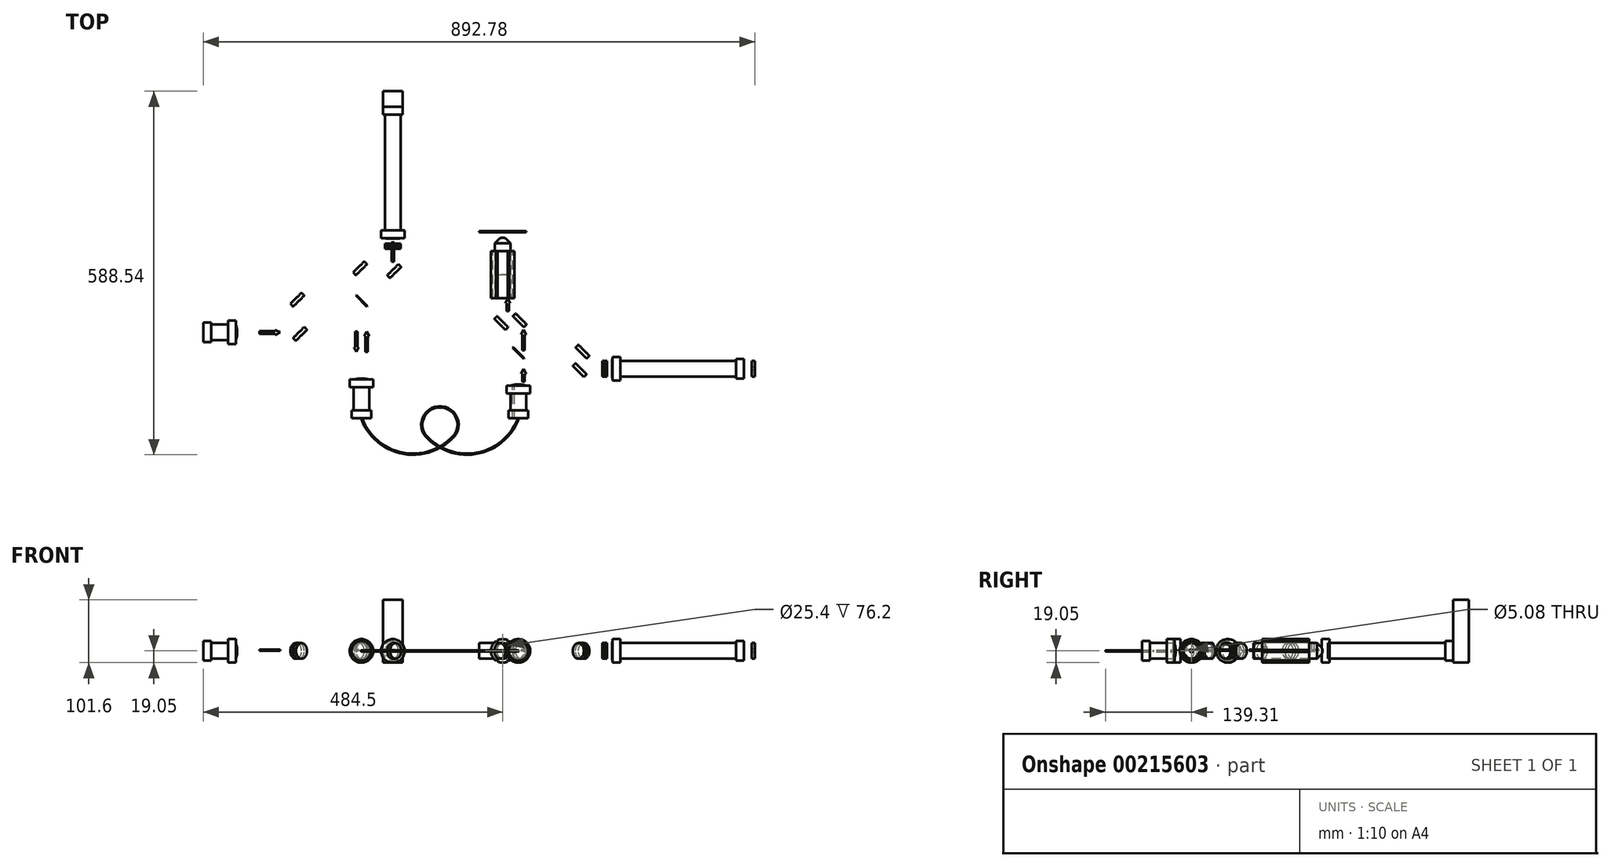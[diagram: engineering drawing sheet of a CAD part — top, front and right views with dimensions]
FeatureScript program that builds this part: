
annotation { "Feature Type Name" : "Feature", "Feature Type Description" : "" }
export const myFeature = defineFeature(function(context is Context, id is Id, definition is map)
    precondition{}
    {
        {
            var Q0;
            Q0=qCreatedBy(makeId("Top.planeOp"),FACE);
            var sketch = newSketch(context, id + "F0", { "sketchPlane" : qUnion([Q0])});
            skLineSegment(sketch, "E0", {"start": v(-101.6, 0) * mm, "end": v(0, 0) * mm, "construction": true});
            skLineSegment(sketch, "E1", {"start": v(0, 0) * mm, "end": v(0, 50.8) * mm});
            skLineSegment(sketch, "E2", {"start": v(0, 50.8) * mm, "end": v(101.6, 50.8) * mm});
            skLineSegment(sketch, "E3", {"start": v(101.6, 50.8) * mm, "end": v(101.6, -76.2) * mm, "construction": true});
            skLineSegment(sketch, "E4", {"start": v(101.6, 50.8) * mm, "end": v(101.6, 101.6) * mm, "construction": true});
            skLineSegment(sketch, "E5", {"start": v(101.6, 101.6) * mm, "end": v(152.4, 101.6) * mm, "construction": true});
            skLineSegment(sketch, "E6", {"start": v(152.4, 101.6) * mm, "end": v(152.4, 152.4) * mm, "construction": true});
            skLineSegment(sketch, "E7.bottom", {"start": v(-114.3, 19.05) * mm, "end": v(-101.6, 19.05) * mm});
            skLineSegment(sketch, "E7.top", {"start": v(-114.3, -19.05) * mm, "end": v(-101.6, -19.05) * mm, "construction": true});
            skLineSegment(sketch, "E7.left", {"start": v(-114.3, 19.05) * mm, "end": v(-114.3, -19.05) * mm, "construction": true});
            skLineSegment(sketch, "E7.right", {"start": v(-101.6, 19.05) * mm, "end": v(-101.6, -19.05) * mm, "construction": true});
            skLineSegment(sketch, "E8.bottom", {"start": v(-114.3, 12.7) * mm, "end": v(-141.6, 12.7) * mm});
            skLineSegment(sketch, "E8.top", {"start": v(-114.3, -12.7) * mm, "end": v(-141.6, -12.7) * mm, "construction": true});
            skLineSegment(sketch, "E8.left", {"start": v(-114.3, 12.7) * mm, "end": v(-114.3, -12.7) * mm});
            skLineSegment(sketch, "E8.right", {"start": v(-141.6, 12.7) * mm, "end": v(-141.6, -12.7) * mm});
            skLineSegment(sketch, "E9.bottom", {"start": v(-154.3, 15.88) * mm, "end": v(-141.6, 15.88) * mm});
            skLineSegment(sketch, "E9.top", {"start": v(-154.3, -15.87) * mm, "end": v(-141.6, -15.87) * mm, "construction": true});
            skLineSegment(sketch, "E9.left", {"start": v(-154.3, 15.88) * mm, "end": v(-154.3, -15.87) * mm, "construction": true});
            skLineSegment(sketch, "E9.right", {"start": v(-141.6, 15.88) * mm, "end": v(-141.6, -15.87) * mm, "construction": true});
            skLineSegment(sketch, "E10.bottom", {"start": v(82.55, -88.9) * mm, "end": v(82.55, -76.2) * mm, "construction": true});
            skLineSegment(sketch, "E10.top", {"start": v(120.65, -88.9) * mm, "end": v(120.65, -76.2) * mm, "construction": true});
            skLineSegment(sketch, "E10.left", {"start": v(82.55, -88.9) * mm, "end": v(120.65, -88.9) * mm, "construction": true});
            skLineSegment(sketch, "E10.right", {"start": v(82.55, -76.2) * mm, "end": v(120.65, -76.2) * mm, "construction": true});
            skLineSegment(sketch, "E11.bottom", {"start": v(88.9, -88.9) * mm, "end": v(88.9, -126.2) * mm, "construction": true});
            skLineSegment(sketch, "E11.top", {"start": v(114.3, -88.9) * mm, "end": v(114.3, -126.2) * mm, "construction": true});
            skLineSegment(sketch, "E11.left", {"start": v(88.9, -88.9) * mm, "end": v(114.3, -88.9) * mm, "construction": true});
            skLineSegment(sketch, "E11.right", {"start": v(88.9, -126.2) * mm, "end": v(114.3, -126.2) * mm, "construction": true});
            skLineSegment(sketch, "E12.bottom", {"start": v(85.73, -138.9) * mm, "end": v(85.73, -126.2) * mm, "construction": true});
            skLineSegment(sketch, "E12.top", {"start": v(117.48, -138.9) * mm, "end": v(117.48, -126.2) * mm, "construction": true});
            skLineSegment(sketch, "E12.left", {"start": v(85.73, -138.9) * mm, "end": v(117.48, -138.9) * mm, "construction": true});
            skLineSegment(sketch, "E12.right", {"start": v(85.73, -126.2) * mm, "end": v(117.48, -126.2) * mm, "construction": true});
            skLineSegment(sketch, "E13.bottom", {"start": v(-8.98, -8.98) * mm, "end": v(8.98, 8.98) * mm});
            skLineSegment(sketch, "E13.top", {"start": v(-6.74, -11.23) * mm, "end": v(11.23, 6.74) * mm});
            skLineSegment(sketch, "E13.left", {"start": v(-8.98, -8.98) * mm, "end": v(-6.74, -11.23) * mm});
            skLineSegment(sketch, "E13.right", {"start": v(8.98, 8.98) * mm, "end": v(11.23, 6.74) * mm});
            skLineSegment(sketch, "E14.bottom", {"start": v(-11.23, 44.06) * mm, "end": v(6.74, 62.03) * mm});
            skLineSegment(sketch, "E14.top", {"start": v(-8.98, 41.82) * mm, "end": v(8.98, 59.78) * mm});
            skLineSegment(sketch, "E14.left", {"start": v(-11.23, 44.06) * mm, "end": v(-8.98, 41.82) * mm});
            skLineSegment(sketch, "E14.right", {"start": v(6.74, 62.03) * mm, "end": v(8.98, 59.78) * mm});
            skLineSegment(sketch, "E15.bottom", {"start": v(93.33, 60.49) * mm, "end": v(111.29, 42.53) * mm});
            skLineSegment(sketch, "E15.top", {"start": v(92.62, 59.78) * mm, "end": v(110.58, 41.82) * mm});
            skLineSegment(sketch, "E15.left", {"start": v(93.33, 60.49) * mm, "end": v(92.62, 59.78) * mm});
            skLineSegment(sketch, "E15.right", {"start": v(111.29, 42.53) * mm, "end": v(110.58, 41.82) * mm});
            skLineSegment(sketch, "E16.bottom", {"start": v(90.37, 94.86) * mm, "end": v(108.34, 112.83) * mm});
            skLineSegment(sketch, "E16.top", {"start": v(92.62, 92.62) * mm, "end": v(110.58, 110.58) * mm});
            skLineSegment(sketch, "E16.left", {"start": v(90.37, 94.86) * mm, "end": v(92.62, 92.62) * mm});
            skLineSegment(sketch, "E16.right", {"start": v(108.34, 112.83) * mm, "end": v(110.58, 110.58) * mm});
            skLineSegment(sketch, "E17.bottom", {"start": v(143.42, 92.62) * mm, "end": v(161.38, 110.58) * mm});
            skLineSegment(sketch, "E17.top", {"start": v(145.66, 90.37) * mm, "end": v(163.63, 108.34) * mm});
            skLineSegment(sketch, "E17.left", {"start": v(143.42, 92.62) * mm, "end": v(145.66, 90.37) * mm});
            skLineSegment(sketch, "E17.right", {"start": v(161.38, 110.58) * mm, "end": v(163.63, 108.34) * mm});
            skLineSegment(sketch, "E18.bottom", {"start": v(171.45, 165.1) * mm, "end": v(171.45, 152.4) * mm, "construction": true});
            skLineSegment(sketch, "E18.top", {"start": v(133.35, 165.1) * mm, "end": v(133.35, 152.4) * mm});
            skLineSegment(sketch, "E18.left", {"start": v(171.45, 165.1) * mm, "end": v(133.35, 165.1) * mm, "construction": true});
            skLineSegment(sketch, "E18.right", {"start": v(171.45, 152.4) * mm, "end": v(133.35, 152.4) * mm, "construction": true});
            skLineSegment(sketch, "E19.bottom", {"start": v(165.1, 165.1) * mm, "end": v(165.1, 352.4) * mm, "construction": true});
            skLineSegment(sketch, "E19.top", {"start": v(139.7, 165.1) * mm, "end": v(139.7, 352.4) * mm, "construction": true});
            skLineSegment(sketch, "E19.left", {"start": v(165.1, 165.1) * mm, "end": v(139.7, 165.1) * mm, "construction": true});
            skLineSegment(sketch, "E19.right", {"start": v(165.1, 352.4) * mm, "end": v(139.7, 352.4) * mm, "construction": true});
            skLineSegment(sketch, "E20.bottom", {"start": v(168.28, 365.1) * mm, "end": v(168.28, 352.4) * mm, "construction": true});
            skLineSegment(sketch, "E20.top", {"start": v(136.53, 365.1) * mm, "end": v(136.53, 352.4) * mm, "construction": true});
            skLineSegment(sketch, "E20.left", {"start": v(168.28, 365.1) * mm, "end": v(136.53, 365.1) * mm, "construction": true});
            skLineSegment(sketch, "E20.right", {"start": v(168.28, 352.4) * mm, "end": v(136.53, 352.4) * mm, "construction": true});
            skLineSegment(sketch, "E21", {"start": v(-101.6, 0) * mm, "end": v(-101.6, 19.05) * mm, "construction": true});
            skLineSegment(sketch, "E22", {"start": v(-101.6, 0) * mm, "end": v(-101.6, 19.05) * mm});
            skLineSegment(sketch, "E23", {"start": v(-114.3, 12.7) * mm, "end": v(-114.3, 19.05) * mm});
            skLineSegment(sketch, "E24", {"start": v(-154.3, 15.88) * mm, "end": v(-154.3, 0) * mm});
            skLineSegment(sketch, "E25", {"start": v(-154.3, 0) * mm, "end": v(-101.6, 0) * mm});
            skLineSegment(sketch, "E26", {"start": v(-141.6, 15.88) * mm, "end": v(-141.6, 12.7) * mm});
            skArc(sketch, "E27", {"start": v(-101.6, -12.7) * mm, "mid": v(-99.53, 0) * mm, "end": v(-101.6, 12.7) * mm, "construction": true});
            skArc(sketch, "E28", {"start": v(-99.53, 0) * mm, "mid": v(-100.05, 6.43) * mm, "end": v(-101.6, 12.7) * mm});
            skLineSegment(sketch, "E29", {"start": v(-99.53, 0) * mm, "end": v(-101.6, 0) * mm});
            skLineSegment(sketch, "E30", {"start": v(101.6, -76.2) * mm, "end": v(120.65, -76.2) * mm, "construction": true});
            skLineSegment(sketch, "E31", {"start": v(120.65, -88.9) * mm, "end": v(114.3, -88.9) * mm, "construction": true});
            skLineSegment(sketch, "E32", {"start": v(101.6, -76.2) * mm, "end": v(120.65, -76.2) * mm});
            skLineSegment(sketch, "E33", {"start": v(120.65, -88.9) * mm, "end": v(114.3, -88.9) * mm});
            skLineSegment(sketch, "E34", {"start": v(114.3, -126.2) * mm, "end": v(114.3, -88.9) * mm});
            skLineSegment(sketch, "E35", {"start": v(114.3, -88.9) * mm, "end": v(120.65, -88.9) * mm});
            skLineSegment(sketch, "E36", {"start": v(120.65, -88.9) * mm, "end": v(120.65, -76.2) * mm});
            skLineSegment(sketch, "E37", {"start": v(114.3, -126.2) * mm, "end": v(117.48, -126.2) * mm});
            skLineSegment(sketch, "E38", {"start": v(117.48, -126.2) * mm, "end": v(117.48, -138.9) * mm});
            skLineSegment(sketch, "E39", {"start": v(117.48, -138.9) * mm, "end": v(101.6, -138.9) * mm});
            skLineSegment(sketch, "E40", {"start": v(101.6, -76.2) * mm, "end": v(101.6, -138.9) * mm});
            skArc(sketch, "E41", {"start": v(114.3, -76.2) * mm, "mid": v(101.6, -74.56) * mm, "end": v(88.9, -76.2) * mm, "construction": true});
            skArc(sketch, "E42", {"start": v(114.3, -76.2) * mm, "mid": v(108, -74.97) * mm, "end": v(101.6, -74.56) * mm});
            skLineSegment(sketch, "E43", {"start": v(101.6, -74.56) * mm, "end": v(101.6, -76.2) * mm});
            skArc(sketch, "E44", {"start": v(152.4, 152) * mm, "mid": v(158.75, 152.1) * mm, "end": v(165.1, 152.4) * mm});
            skLineSegment(sketch, "E45", {"start": v(152.4, 152.4) * mm, "end": v(152.4, 156.02) * mm, "construction": true});
            skLineSegment(sketch, "E46", {"start": v(152.4, 487.9) * mm, "end": v(152.4, 156.02) * mm, "construction": true});
            skLineSegment(sketch, "E47", {"start": v(152.4, 152) * mm, "end": v(152.4, 365.1) * mm});
            skLineSegment(sketch, "E48", {"start": v(152.4, 365.1) * mm, "end": v(168.28, 365.1) * mm});
            skLineSegment(sketch, "E49", {"start": v(168.28, 365.1) * mm, "end": v(168.28, 352.4) * mm});
            skLineSegment(sketch, "E50", {"start": v(168.28, 352.4) * mm, "end": v(165.1, 352.4) * mm});
            skLineSegment(sketch, "E51", {"start": v(165.1, 352.4) * mm, "end": v(165.1, 165.1) * mm});
            skLineSegment(sketch, "E52", {"start": v(165.1, 165.1) * mm, "end": v(171.45, 165.1) * mm});
            skLineSegment(sketch, "E53", {"start": v(171.45, 165.1) * mm, "end": v(171.45, 152.4) * mm});
            skLineSegment(sketch, "E54", {"start": v(171.45, 152.4) * mm, "end": v(165.1, 152.4) * mm});
            skLineSegment(sketch, "E55", {"start": v(101.6, -138.9) * mm, "end": v(101.6, -164.3) * mm, "construction": true});
            skLineSegment(sketch, "E56", {"start": v(101.6, -164.3) * mm, "end": v(355.6, -164.3) * mm, "construction": true});
            skLineSegment(sketch, "E57", {"start": v(355.6, -164.3) * mm, "end": v(355.6, -138.9) * mm, "construction": true});
            skLineSegment(sketch, "E58.bottom", {"start": v(336.55, -98.9) * mm, "end": v(336.55, -86.2) * mm, "construction": true});
            skLineSegment(sketch, "E58.top", {"start": v(374.65, -98.9) * mm, "end": v(374.65, -86.2) * mm, "construction": true});
            skLineSegment(sketch, "E58.left", {"start": v(336.55, -98.9) * mm, "end": v(374.65, -98.9) * mm, "construction": true});
            skLineSegment(sketch, "E58.right", {"start": v(336.55, -86.2) * mm, "end": v(374.65, -86.2) * mm, "construction": true});
            skLineSegment(sketch, "E59.bottom", {"start": v(342.9, -98.9) * mm, "end": v(342.9, -126.2) * mm, "construction": true});
            skLineSegment(sketch, "E59.top", {"start": v(368.3, -98.9) * mm, "end": v(368.3, -126.2) * mm, "construction": true});
            skLineSegment(sketch, "E59.left", {"start": v(342.9, -98.9) * mm, "end": v(368.3, -98.9) * mm, "construction": true});
            skLineSegment(sketch, "E59.right", {"start": v(342.9, -126.2) * mm, "end": v(368.3, -126.2) * mm, "construction": true});
            skLineSegment(sketch, "E60.bottom", {"start": v(339.73, -138.9) * mm, "end": v(339.73, -126.2) * mm, "construction": true});
            skLineSegment(sketch, "E60.top", {"start": v(371.48, -138.9) * mm, "end": v(371.48, -126.2) * mm, "construction": true});
            skLineSegment(sketch, "E60.left", {"start": v(339.73, -138.9) * mm, "end": v(371.48, -138.9) * mm, "construction": true});
            skLineSegment(sketch, "E60.right", {"start": v(339.73, -126.2) * mm, "end": v(371.48, -126.2) * mm, "construction": true});
            skLineSegment(sketch, "E61", {"start": v(355.6, -86.2) * mm, "end": v(374.65, -86.2) * mm, "construction": true});
            skLineSegment(sketch, "E62", {"start": v(374.65, -98.9) * mm, "end": v(368.3, -98.9) * mm, "construction": true});
            skLineSegment(sketch, "E63", {"start": v(355.6, -86.2) * mm, "end": v(374.65, -86.2) * mm});
            skLineSegment(sketch, "E64", {"start": v(374.65, -98.9) * mm, "end": v(368.3, -98.9) * mm});
            skLineSegment(sketch, "E65", {"start": v(368.3, -126.2) * mm, "end": v(368.3, -98.9) * mm});
            skLineSegment(sketch, "E66", {"start": v(368.3, -98.9) * mm, "end": v(374.65, -98.9) * mm});
            skLineSegment(sketch, "E67", {"start": v(374.65, -98.9) * mm, "end": v(374.65, -86.2) * mm});
            skLineSegment(sketch, "E68", {"start": v(368.3, -126.2) * mm, "end": v(371.48, -126.2) * mm});
            skLineSegment(sketch, "E69", {"start": v(371.48, -126.2) * mm, "end": v(371.48, -138.9) * mm});
            skLineSegment(sketch, "E70", {"start": v(371.48, -138.9) * mm, "end": v(355.6, -138.9) * mm});
            skLineSegment(sketch, "E71", {"start": v(355.6, -86.2) * mm, "end": v(355.6, -138.9) * mm});
            skArc(sketch, "E72", {"start": v(368.3, -86.2) * mm, "mid": v(355.6, -84.13) * mm, "end": v(342.9, -86.2) * mm, "construction": true});
            skArc(sketch, "E73", {"start": v(368.3, -86.2) * mm, "mid": v(362.03, -84.65) * mm, "end": v(355.6, -84.13) * mm});
            skLineSegment(sketch, "E74", {"start": v(355.6, -84.13) * mm, "end": v(355.6, -86.2) * mm});
            skLineSegment(sketch, "E75", {"start": v(355.6, -84.13) * mm, "end": v(355.6, -33.33) * mm, "construction": true});
            skLineSegment(sketch, "E76", {"start": v(355.6, -33.33) * mm, "end": v(457.2, -33.33) * mm, "construction": true});
            skLineSegment(sketch, "E77", {"start": v(457.2, -33.33) * mm, "end": v(457.2, -58.73) * mm, "construction": true});
            skLineSegment(sketch, "E78", {"start": v(457.2, -58.73) * mm, "end": v(508, -58.73) * mm, "construction": true});
            skLineSegment(sketch, "E79", {"start": v(355.6, -33.33) * mm, "end": v(355.6, 17.47) * mm, "construction": true});
            skLineSegment(sketch, "E80", {"start": v(355.6, 17.47) * mm, "end": v(330.2, 17.47) * mm, "construction": true});
            skLineSegment(sketch, "E81", {"start": v(330.2, 17.47) * mm, "end": v(330.2, 220.67) * mm, "construction": true});
            skLineSegment(sketch, "E82.bottom", {"start": v(520.7, -77.78) * mm, "end": v(508, -77.78) * mm, "construction": true});
            skLineSegment(sketch, "E82.top", {"start": v(520.7, -39.68) * mm, "end": v(508, -39.68) * mm});
            skLineSegment(sketch, "E82.left", {"start": v(520.7, -77.78) * mm, "end": v(520.7, -39.68) * mm, "construction": true});
            skLineSegment(sketch, "E82.right", {"start": v(508, -77.78) * mm, "end": v(508, -39.68) * mm, "construction": true});
            skLineSegment(sketch, "E83.bottom", {"start": v(520.7, -71.43) * mm, "end": v(708, -71.43) * mm, "construction": true});
            skLineSegment(sketch, "E83.top", {"start": v(520.7, -46.03) * mm, "end": v(708, -46.03) * mm, "construction": true});
            skLineSegment(sketch, "E83.left", {"start": v(520.7, -71.43) * mm, "end": v(520.7, -46.03) * mm, "construction": true});
            skLineSegment(sketch, "E83.right", {"start": v(708, -71.43) * mm, "end": v(708, -46.03) * mm, "construction": true});
            skLineSegment(sketch, "E84.bottom", {"start": v(720.7, -74.6) * mm, "end": v(708, -74.6) * mm, "construction": true});
            skLineSegment(sketch, "E84.top", {"start": v(720.7, -42.86) * mm, "end": v(708, -42.86) * mm, "construction": true});
            skLineSegment(sketch, "E84.left", {"start": v(720.7, -74.6) * mm, "end": v(720.7, -42.86) * mm, "construction": true});
            skLineSegment(sketch, "E84.right", {"start": v(708, -74.6) * mm, "end": v(708, -42.86) * mm, "construction": true});
            skLineSegment(sketch, "E85", {"start": v(720.7, -58.73) * mm, "end": v(720.7, -74.6) * mm});
            skLineSegment(sketch, "E86", {"start": v(720.7, -74.6) * mm, "end": v(708, -74.6) * mm});
            skLineSegment(sketch, "E87", {"start": v(708, -74.6) * mm, "end": v(708, -71.43) * mm});
            skLineSegment(sketch, "E88", {"start": v(708, -71.43) * mm, "end": v(520.7, -71.43) * mm});
            skLineSegment(sketch, "E89", {"start": v(520.7, -71.43) * mm, "end": v(520.7, -77.78) * mm});
            skLineSegment(sketch, "E90", {"start": v(520.7, -77.78) * mm, "end": v(508, -77.78) * mm});
            skArc(sketch, "E91", {"start": v(507.1, -58.73) * mm, "mid": v(507.32, -68.27) * mm, "end": v(508, -77.78) * mm});
            skLineSegment(sketch, "E92", {"start": v(508, -58.73) * mm, "end": v(765.02, -58.73) * mm, "construction": true});
            skLineSegment(sketch, "E93", {"start": v(508, -58.73) * mm, "end": v(507.1, -58.73) * mm});
            skLineSegment(sketch, "E94", {"start": v(720.7, -58.73) * mm, "end": v(507.1, -58.73) * mm});
            skLineSegment(sketch, "E95", {"start": v(448.22, -24.35) * mm, "end": v(466.18, -42.31) * mm});
            skLineSegment(sketch, "E96", {"start": v(448.22, -49.75) * mm, "end": v(466.18, -67.71) * mm});
            skLineSegment(sketch, "E97", {"start": v(364.58, -42.31) * mm, "end": v(346.62, -24.35) * mm});
            skLineSegment(sketch, "E98", {"start": v(346.62, 26.45) * mm, "end": v(364.58, 8.49) * mm});
            skLineSegment(sketch, "E99", {"start": v(321.22, 26.45) * mm, "end": v(339.18, 8.49) * mm});
            skLineSegment(sketch, "E100.bottom", {"start": v(342.9, 131.77) * mm, "end": v(317.5, 131.77) * mm});
            skLineSegment(sketch, "E100.top", {"start": v(342.9, 55.57) * mm, "end": v(317.5, 55.57) * mm});
            skLineSegment(sketch, "E100.left", {"start": v(342.9, 131.77) * mm, "end": v(342.9, 55.57) * mm});
            skLineSegment(sketch, "E100.right", {"start": v(317.5, 131.77) * mm, "end": v(317.5, 55.57) * mm});
            skPoint(sketch, "E100.middle", {"position": v(330.2, 93.67) * mm});
            skLineSegment(sketch, "E101.bottom", {"start": v(349.25, 131.77) * mm, "end": v(311.15, 131.77) * mm});
            skLineSegment(sketch, "E101.top", {"start": v(349.25, 55.57) * mm, "end": v(311.15, 55.57) * mm});
            skLineSegment(sketch, "E101.left", {"start": v(349.25, 131.77) * mm, "end": v(349.25, 55.57) * mm});
            skLineSegment(sketch, "E101.right", {"start": v(311.15, 131.77) * mm, "end": v(311.15, 55.57) * mm});
            skLineSegment(sketch, "E102.bottom", {"start": v(342.9, 93.67) * mm, "end": v(317.5, 93.67) * mm, "construction": true});
            skLineSegment(sketch, "E102.top", {"start": v(342.9, 144.47) * mm, "end": v(317.5, 144.47) * mm, "construction": true});
            skLineSegment(sketch, "E102.left", {"start": v(342.9, 93.67) * mm, "end": v(342.9, 144.47) * mm, "construction": true});
            skLineSegment(sketch, "E102.right", {"start": v(317.5, 93.67) * mm, "end": v(317.5, 144.47) * mm, "construction": true});
            skPoint(sketch, "E102.middle", {"position": v(330.2, 119.07) * mm});
            skLineSegment(sketch, "E103", {"start": v(317.5, 144.47) * mm, "end": v(323.91, 150.88) * mm, "construction": true});
            skLineSegment(sketch, "E104", {"start": v(336.49, 150.88) * mm, "end": v(342.9, 144.47) * mm, "construction": true});
            skPoint(sketch, "E105.visualSharp", {"position": v(330.2, 157.17) * mm});
            skArc(sketch, "E105.filletArc", {"start": v(336.49, 150.88) * mm, "mid": v(330.2, 153.49) * mm, "end": v(323.91, 150.88) * mm, "construction": true});
            skLineSegment(sketch, "E106", {"start": v(330.2, 93.67) * mm, "end": v(317.5, 93.67) * mm});
            skLineSegment(sketch, "E107", {"start": v(317.5, 93.67) * mm, "end": v(317.5, 144.47) * mm});
            skLineSegment(sketch, "E108", {"start": v(317.5, 144.47) * mm, "end": v(323.91, 150.88) * mm});
            skArc(sketch, "E109", {"start": v(330.2, 153.49) * mm, "mid": v(326.8, 152.81) * mm, "end": v(323.91, 150.88) * mm});
            skLineSegment(sketch, "E110", {"start": v(330.2, 93.67) * mm, "end": v(330.2, 153.49) * mm});
            skLineSegment(sketch, "E111", {"start": v(292.1, 162.38) * mm, "end": v(368.3, 162.38) * mm});
            skArc(sketch, "E112", {"start": v(101.6, -138.9) * mm, "mid": v(170.42, -195.9) * mm, "end": v(254, -164.3) * mm});
            skArc(sketch, "E113", {"start": v(203.2, -164.3) * mm, "mid": v(286.78, -195.9) * mm, "end": v(355.6, -138.9) * mm});
            skCircle(sketch, "E114", {"center": v(228.6, -149.66) * mm, "radius": 29.32 * mm, "construction": true});
            skPoint(sketch, "E114.third.point", {"position": v(244.49, -174.3) * mm});
            skArc(sketch, "E115", {"start": v(254, -164.3) * mm, "mid": v(228.6, -120.34) * mm, "end": v(203.2, -164.3) * mm});
            skLineSegment(sketch, "E116", {"start": v(-63.5, 0) * mm, "end": v(-63.5, -2) * mm});
            skLineSegment(sketch, "E117", {"start": v(-63.5, -2) * mm, "end": v(-38.1, -2) * mm});
            skLineSegment(sketch, "E118", {"start": v(-38.1, -2) * mm, "end": v(-38.1, -4) * mm});
            skLineSegment(sketch, "E119", {"start": v(-38.1, -4) * mm, "end": v(-30.1, 0) * mm});
            skLineSegment(sketch, "E120.MirrorCS", {"start": v(-63.5, 0) * mm, "end": v(-63.5, 2) * mm});
            skLineSegment(sketch, "E121.MirrorCS", {"start": v(-63.5, 2) * mm, "end": v(-38.1, 2) * mm});
            skLineSegment(sketch, "E122.MirrorCS", {"start": v(-38.1, 2) * mm, "end": v(-38.1, 4) * mm});
            skLineSegment(sketch, "E123.MirrorCS", {"start": v(-38.1, 4) * mm, "end": v(-30.1, 0) * mm});
            skLineSegment(sketch, "E124", {"start": v(109.95, 1.65) * mm, "end": v(109.95, -31.75) * mm, "construction": true});
            skLineSegment(sketch, "E125", {"start": v(109.95, 1.65) * mm, "end": v(113.95, -6.35) * mm});
            skLineSegment(sketch, "E126", {"start": v(113.95, -6.35) * mm, "end": v(111.95, -6.35) * mm});
            skLineSegment(sketch, "E127", {"start": v(111.95, -6.35) * mm, "end": v(111.95, -31.75) * mm});
            skLineSegment(sketch, "E128", {"start": v(111.95, -31.75) * mm, "end": v(107.95, -31.75) * mm});
            skLineSegment(sketch, "E129", {"start": v(107.95, -31.75) * mm, "end": v(107.95, -6.35) * mm});
            skLineSegment(sketch, "E130", {"start": v(107.95, -6.35) * mm, "end": v(105.95, -6.35) * mm});
            skLineSegment(sketch, "E131", {"start": v(105.95, -6.35) * mm, "end": v(109.95, 1.65) * mm});
            skLineSegment(sketch, "E132", {"start": v(93.25, -31.75) * mm, "end": v(93.25, 1.65) * mm, "construction": true});
            skLineSegment(sketch, "E133", {"start": v(93.25, -31.75) * mm, "end": v(89.25, -23.75) * mm});
            skLineSegment(sketch, "E134", {"start": v(89.25, -23.75) * mm, "end": v(91.25, -23.75) * mm});
            skLineSegment(sketch, "E135", {"start": v(91.25, -23.75) * mm, "end": v(91.25, 1.65) * mm});
            skLineSegment(sketch, "E136", {"start": v(91.25, 1.65) * mm, "end": v(95.25, 1.65) * mm});
            skLineSegment(sketch, "E137", {"start": v(95.25, 1.65) * mm, "end": v(95.25, -23.75) * mm});
            skLineSegment(sketch, "E138", {"start": v(95.25, -23.75) * mm, "end": v(97.25, -23.75) * mm});
            skLineSegment(sketch, "E139", {"start": v(97.25, -23.75) * mm, "end": v(93.25, -31.75) * mm});
            skLineSegment(sketch, "E140", {"start": v(152.4, 147.7) * mm, "end": v(152.4, 114.3) * mm, "construction": true});
            skLineSegment(sketch, "E141", {"start": v(152.4, 147.7) * mm, "end": v(156.4, 139.7) * mm});
            skLineSegment(sketch, "E142", {"start": v(156.4, 139.7) * mm, "end": v(154.4, 139.7) * mm});
            skLineSegment(sketch, "E143", {"start": v(154.4, 139.7) * mm, "end": v(154.4, 114.3) * mm});
            skLineSegment(sketch, "E144", {"start": v(154.4, 114.3) * mm, "end": v(150.4, 114.3) * mm});
            skLineSegment(sketch, "E145", {"start": v(150.4, 114.3) * mm, "end": v(150.4, 139.7) * mm});
            skLineSegment(sketch, "E146", {"start": v(150.4, 139.7) * mm, "end": v(148.4, 139.7) * mm});
            skLineSegment(sketch, "E147", {"start": v(148.4, 139.7) * mm, "end": v(152.4, 147.7) * mm});
            skLineSegment(sketch, "E148", {"start": v(363.95, -58.73) * mm, "end": v(363.95, -79.43) * mm, "construction": true});
            skLineSegment(sketch, "E149", {"start": v(363.95, -58.73) * mm, "end": v(367.95, -66.73) * mm});
            skLineSegment(sketch, "E150", {"start": v(367.95, -66.73) * mm, "end": v(365.95, -66.73) * mm});
            skLineSegment(sketch, "E151", {"start": v(365.95, -66.73) * mm, "end": v(365.95, -79.43) * mm});
            skLineSegment(sketch, "E152", {"start": v(365.95, -79.43) * mm, "end": v(361.95, -79.43) * mm});
            skLineSegment(sketch, "E153", {"start": v(361.95, -79.43) * mm, "end": v(361.95, -66.73) * mm});
            skLineSegment(sketch, "E154", {"start": v(361.95, -66.73) * mm, "end": v(359.95, -66.73) * mm});
            skLineSegment(sketch, "E155", {"start": v(359.95, -66.73) * mm, "end": v(363.95, -58.73) * mm});
            skLineSegment(sketch, "E156", {"start": v(363.95, 4.77) * mm, "end": v(363.95, -28.63) * mm, "construction": true});
            skLineSegment(sketch, "E157", {"start": v(363.95, 4.77) * mm, "end": v(367.95, -3.23) * mm});
            skLineSegment(sketch, "E158", {"start": v(367.95, -3.23) * mm, "end": v(365.95, -3.23) * mm});
            skLineSegment(sketch, "E159", {"start": v(365.95, -3.23) * mm, "end": v(365.95, -28.63) * mm});
            skLineSegment(sketch, "E160", {"start": v(365.95, -28.63) * mm, "end": v(361.95, -28.63) * mm});
            skLineSegment(sketch, "E161", {"start": v(361.95, -28.63) * mm, "end": v(361.95, -3.23) * mm});
            skLineSegment(sketch, "E162", {"start": v(361.95, -3.23) * mm, "end": v(359.95, -3.23) * mm});
            skLineSegment(sketch, "E163", {"start": v(359.95, -3.23) * mm, "end": v(363.95, 4.77) * mm});
            skLineSegment(sketch, "E164", {"start": v(338.55, 55.57) * mm, "end": v(338.55, 34.87) * mm, "construction": true});
            skLineSegment(sketch, "E165", {"start": v(338.55, 55.57) * mm, "end": v(342.55, 47.57) * mm});
            skLineSegment(sketch, "E166", {"start": v(342.55, 47.57) * mm, "end": v(340.55, 47.57) * mm});
            skLineSegment(sketch, "E167", {"start": v(340.55, 47.57) * mm, "end": v(340.55, 34.87) * mm});
            skLineSegment(sketch, "E168", {"start": v(340.55, 34.87) * mm, "end": v(336.55, 34.87) * mm});
            skLineSegment(sketch, "E169", {"start": v(336.55, 34.87) * mm, "end": v(336.55, 47.57) * mm});
            skLineSegment(sketch, "E170", {"start": v(336.55, 47.57) * mm, "end": v(334.55, 47.57) * mm});
            skLineSegment(sketch, "E171", {"start": v(334.55, 47.57) * mm, "end": v(338.55, 55.57) * mm});
            skSolve(sketch);
        }
        {
            var Q0;
            {var subQ1=sQuery(id+"F0.wireOp",EDGE,"E7.bottom");Q0=makeQuery(id+"F0.imprint","IMPRINT",FACE,{"disambiguationData":[TD([[makeQuery(id+"F0.imprint","IMPRINT",EDGE,{"derivedFrom":subQ1}),-1.0]])]});}
            var Q1;
            {var subQ0=sQuery(id+"F0.wireOp",EDGE,"E8.bottom");Q1=makeQuery(id+"F0.imprint","IMPRINT",FACE,{"disambiguationData":[TD([[makeQuery(id+"F0.imprint","IMPRINT",EDGE,{"derivedFrom":subQ0}),1.0]])]});}
            var Q2;
            Q2=makeQuery(id+"F0.imprint","IMPRINT",FACE,{"disambiguationData":[TD([[makeQuery(id+"F0.imprint","IMPRINT",EDGE,{"derivedFrom":sQuery(id+"F0.wireOp",EDGE,"E9.bottom")}),-1.0]])]});
            var Q3;
            {var subQ2=sQuery(id+"F0.wireOp",EDGE,"E28");Q3=makeQuery(id+"F0.imprint","IMPRINT",FACE,{"disambiguationData":[TD([[makeQuery(id+"F0.imprint","IMPRINT",EDGE,{"derivedFrom":subQ2}),1.0]])]});}
            var Q4;
            Q4=sQuery(id+"F0.wireOp",EDGE,"E0");
            revolve(context, id + "F1", {"entities" : qUnion([Q0, Q1, Q2, Q3]), "axis" : qUnion([Q4]), "revolveType" : RevolveType.FULL});
        }
        {
            var Q0;
            Q0=sQuery(id+"F0.wireOp",EDGE,"E13.bottom");
            cPlane(context, id + "F2", {"entities" : qUnion([Q0]), "cplaneType" : CPlaneType.LINE_ANGLE, "offset" : 25.4 * mm, "angle" : 90 * degree, "width" : 152.4 * mm, "height" : 152.4 * mm});
        }
        {
            var Q0;
            Q0=qCreatedBy(id+"F2.planeOp",FACE);
            var sketch = newSketch(context, id + "F3", { "sketchPlane" : qUnion([Q0])});
            skCircle(sketch, "E172", {"center": v(0, 0) * mm, "radius": 12.7 * mm});
            skSolve(sketch);
        }
        {
            var Q0;
            Q0=makeQuery(id+"F3.imprint","IMPRINT",FACE,{"disambiguationData":[TD([[makeQuery(id+"F3.imprint","IMPRINT",EDGE,{"derivedFrom":sQuery(id+"F3.wireOp",EDGE,"E172")}),1.0]])]});
            extrude(context, id + "F4", {"entities" : qUnion([Q0]), "depth" : 6.35 * mm});
        }
        {
            var Q0;
            Q0=sQuery(id+"F0.wireOp",EDGE,"E14.top");
            cPlane(context, id + "F5", {"entities" : qUnion([Q0]), "cplaneType" : CPlaneType.LINE_ANGLE, "offset" : 25.4 * mm, "angle" : 90 * degree, "width" : 152.4 * mm, "height" : 152.4 * mm});
        }
        {
            var Q0;
            Q0=qCreatedBy(id+"F5.planeOp",FACE);
            var sketch = newSketch(context, id + "F6", { "sketchPlane" : qUnion([Q0])});
            skCircle(sketch, "E173", {"center": v(35.92, 0) * mm, "radius": 12.7 * mm});
            skSolve(sketch);
        }
        {
            var Q0;
            Q0=makeQuery(id+"F6.imprint","IMPRINT",FACE,{"disambiguationData":[TD([[makeQuery(id+"F6.imprint","IMPRINT",EDGE,{"derivedFrom":sQuery(id+"F6.wireOp",EDGE,"E173")}),1.0]])]});
            extrude(context, id + "F7", {"entities" : qUnion([Q0]), "oppositeDirection" : true, "depth" : 6.35 * mm});
        }
        {
            var Q0;
            Q0=makeQuery(id+"F0.imprint","IMPRINT",FACE,{"disambiguationData":[TD([[makeQuery(id+"F0.imprint","IMPRINT",EDGE,{"derivedFrom":sQuery(id+"F0.wireOp",EDGE,"E15.bottom")}),-1.0]])]});
            extrude(context, id + "F8", {"entities" : qUnion([Q0]), "endBound" : BoundingType.SYMMETRIC, "depth" : 25.4 * mm});
        }
        {
            var Q0;
            Q0=makeQuery(id+"F0.imprint","IMPRINT",FACE,{"disambiguationData":[TD([[makeQuery(id+"F0.imprint","IMPRINT",EDGE,{"derivedFrom":sQuery(id+"F0.wireOp",EDGE,"E32")}),-1.0]])]});
            var Q1;
            {var subQ2=sQuery(id+"F0.wireOp",EDGE,"E42");Q1=makeQuery(id+"F0.imprint","IMPRINT",FACE,{"disambiguationData":[TD([[makeQuery(id+"F0.imprint","IMPRINT",EDGE,{"derivedFrom":subQ2}),1.0]])]});}
            var Q2;
            Q2=sQuery(id+"F0.wireOp",EDGE,"E3");
            revolve(context, id + "F9", {"entities" : qUnion([Q0, Q1]), "axis" : qUnion([Q2]), "revolveType" : RevolveType.FULL});
        }
        {
            var Q0;
            Q0=sQuery(id+"F0.wireOp",EDGE,"E16.top");
            cPlane(context, id + "F10", {"entities" : qUnion([Q0]), "cplaneType" : CPlaneType.LINE_ANGLE, "offset" : 25.4 * mm, "angle" : 90 * degree, "width" : 152.4 * mm, "height" : 152.4 * mm});
        }
        {
            var Q0;
            Q0=qCreatedBy(id+"F10.planeOp",FACE);
            var sketch = newSketch(context, id + "F11", { "sketchPlane" : qUnion([Q0])});
            skCircle(sketch, "E174", {"center": v(143.68, 0) * mm, "radius": 12.7 * mm});
            skSolve(sketch);
        }
        {
            var Q0;
            Q0=makeQuery(id+"F11.imprint","IMPRINT",FACE,{"disambiguationData":[TD([[makeQuery(id+"F11.imprint","IMPRINT",EDGE,{"derivedFrom":sQuery(id+"F11.wireOp",EDGE,"E174")}),1.0]])]});
            extrude(context, id + "F12", {"entities" : qUnion([Q0]), "oppositeDirection" : true, "depth" : 6.35 * mm});
        }
        {
            var Q0;
            Q0=sQuery(id+"F0.wireOp",EDGE,"E17.bottom");
            cPlane(context, id + "F13", {"entities" : qUnion([Q0]), "cplaneType" : CPlaneType.LINE_ANGLE, "offset" : 25.4 * mm, "angle" : 90 * degree, "width" : 152.4 * mm, "height" : 152.4 * mm});
        }
        {
            var Q0;
            Q0=qCreatedBy(id+"F13.planeOp",FACE);
            var sketch = newSketch(context, id + "F14", { "sketchPlane" : qUnion([Q0])});
            skCircle(sketch, "E175", {"center": v(179.6, 0) * mm, "radius": 12.7 * mm});
            skSolve(sketch);
        }
        {
            var Q0;
            Q0=makeQuery(id+"F14.imprint","IMPRINT",FACE,{"disambiguationData":[TD([[makeQuery(id+"F14.imprint","IMPRINT",EDGE,{"derivedFrom":sQuery(id+"F14.wireOp",EDGE,"E175")}),1.0]])]});
            extrude(context, id + "F15", {"entities" : qUnion([Q0]), "depth" : 6.35 * mm});
        }
        {
            var Q0;
            Q0=makeQuery(id+"F0.imprint","IMPRINT",FACE,{"disambiguationData":[TD([[makeQuery(id+"F0.imprint","IMPRINT",EDGE,{"derivedFrom":sQuery(id+"F0.wireOp",EDGE,"E44")}),1.0]])]});
            var Q1;
            Q1=sQuery(id+"F0.wireOp",EDGE,"E6");
            revolve(context, id + "F16", {"entities" : qUnion([Q0]), "axis" : qUnion([Q1]), "revolveType" : RevolveType.FULL});
        }
        {
            var Q0;
            Q0=makeQuery(id+"F16.opRevolve","SWEPT_FACE",FACE,{"disambiguationData":[OSD([sQuery(id+"F0.wireOp",EDGE,"E48")])]});
            var sketch = newSketch(context, id + "F17", { "sketchPlane" : qUnion([Q0])});
            skLineSegment(sketch, "E176.bottom", {"start": v(-168.28, 82.55) * mm, "end": v(-136.53, 82.55) * mm});
            skLineSegment(sketch, "E176.top", {"start": v(-168.28, -19.05) * mm, "end": v(-136.53, -19.05) * mm});
            skLineSegment(sketch, "E176.left", {"start": v(-168.28, 82.55) * mm, "end": v(-168.28, -19.05) * mm});
            skLineSegment(sketch, "E176.right", {"start": v(-136.53, 82.55) * mm, "end": v(-136.53, -19.05) * mm});
            skSolve(sketch);
        }
        {
            var Q0;
            Q0 = qSketchRegion(id + "F17", true);
            extrude(context, id + "F18", {"entities" : qUnion([Q0]), "depth" : 25.4 * mm});
        }
        {
            var Q0;
            {var subQ3=sQuery(id+"F0.wireOp",EDGE,"E85");Q0=makeQuery(id+"F0.imprint","IMPRINT",FACE,{"disambiguationData":[TD([[makeQuery(id+"F0.imprint","IMPRINT",EDGE,{"derivedFrom":subQ3}),-1.0]])]});}
            var Q1;
            Q1=sQuery(id+"F0.wireOp",EDGE,"E78");
            revolve(context, id + "F19", {"entities" : qUnion([Q0]), "axis" : qUnion([Q1]), "revolveType" : RevolveType.FULL});
        }
        {
            var Q0;
            {var subQ2=sQuery(id+"F0.wireOp",EDGE,"E73");Q0=makeQuery(id+"F0.imprint","IMPRINT",FACE,{"disambiguationData":[TD([[makeQuery(id+"F0.imprint","IMPRINT",EDGE,{"derivedFrom":subQ2}),1.0]])]});}
            var Q1;
            Q1=makeQuery(id+"F0.imprint","IMPRINT",FACE,{"disambiguationData":[TD([[makeQuery(id+"F0.imprint","IMPRINT",EDGE,{"derivedFrom":sQuery(id+"F0.wireOp",EDGE,"E65")}),1.0]])]});
            var Q2;
            Q2=sQuery(id+"F0.wireOp",EDGE,"E75");
            revolve(context, id + "F20", {"entities" : qUnion([Q0, Q1]), "axis" : qUnion([Q2]), "revolveType" : RevolveType.FULL});
        }
        {
            var Q0;
            Q0=sQuery(id+"F0.wireOp",EDGE,"E98");
            cPlane(context, id + "F21", {"entities" : qUnion([Q0]), "cplaneType" : CPlaneType.LINE_ANGLE, "offset" : 25.4 * mm, "angle" : 90 * degree, "width" : 152.4 * mm, "height" : 152.4 * mm});
        }
        {
            var Q0;
            Q0=qCreatedBy(id+"F21.planeOp",FACE);
            var sketch = newSketch(context, id + "F22", { "sketchPlane" : qUnion([Q0])});
            skCircle(sketch, "E177", {"center": v(-239.1, 0) * mm, "radius": 12.7 * mm});
            skSolve(sketch);
        }
        {
            var Q0;
            Q0=sQuery(id+"F0.wireOp",EDGE,"E99");
            cPlane(context, id + "F23", {"entities" : qUnion([Q0]), "cplaneType" : CPlaneType.LINE_ANGLE, "offset" : 25.4 * mm, "angle" : 90 * degree, "width" : 152.4 * mm, "height" : 152.4 * mm});
        }
        {
            var Q0;
            Q0=qCreatedBy(id+"F23.planeOp",FACE);
            var sketch = newSketch(context, id + "F24", { "sketchPlane" : qUnion([Q0])});
            skCircle(sketch, "E178", {"center": v(-221.13, 0) * mm, "radius": 12.7 * mm});
            skSolve(sketch);
        }
        {
            var Q0;
            Q0=makeQuery(id+"F24.imprint","IMPRINT",FACE,{"disambiguationData":[TD([[makeQuery(id+"F24.imprint","IMPRINT",EDGE,{"derivedFrom":sQuery(id+"F24.wireOp",EDGE,"E178")}),1.0]])]});
            extrude(context, id + "F25", {"entities" : qUnion([Q0]), "oppositeDirection" : true, "depth" : 6.35 * mm});
        }
        {
            var Q0;
            Q0=makeQuery(id+"F22.imprint","IMPRINT",FACE,{"disambiguationData":[TD([[makeQuery(id+"F22.imprint","IMPRINT",EDGE,{"derivedFrom":sQuery(id+"F22.wireOp",EDGE,"E177")}),1.0]])]});
            extrude(context, id + "F26", {"entities" : qUnion([Q0]), "depth" : 6.35 * mm});
        }
        {
            var Q0;
            Q0=sQuery(id+"F0.wireOp",EDGE,"E95");
            cPlane(context, id + "F27", {"entities" : qUnion([Q0]), "cplaneType" : CPlaneType.LINE_ANGLE, "offset" : 25.4 * mm, "angle" : 90 * degree, "width" : 152.4 * mm, "height" : 152.4 * mm});
        }
        {
            var Q0;
            Q0=qCreatedBy(id+"F27.planeOp",FACE);
            var sketch = newSketch(context, id + "F28", { "sketchPlane" : qUnion([Q0])});
            skCircle(sketch, "E179", {"center": v(-346.86, 0) * mm, "radius": 12.7 * mm});
            skSolve(sketch);
        }
        {
            var Q0;
            Q0=makeQuery(id+"F28.imprint","IMPRINT",FACE,{"disambiguationData":[TD([[makeQuery(id+"F28.imprint","IMPRINT",EDGE,{"derivedFrom":sQuery(id+"F28.wireOp",EDGE,"E179")}),1.0]])]});
            extrude(context, id + "F29", {"entities" : qUnion([Q0]), "depth" : 6.35 * mm});
        }
        {
            var Q0;
            Q0=sQuery(id+"F0.wireOp",EDGE,"E96");
            cPlane(context, id + "F30", {"entities" : qUnion([Q0]), "cplaneType" : CPlaneType.LINE_ANGLE, "offset" : 25.4 * mm, "angle" : 90 * degree, "width" : 152.4 * mm, "height" : 152.4 * mm});
        }
        {
            var Q0;
            Q0=qCreatedBy(id+"F30.planeOp",FACE);
            var sketch = newSketch(context, id + "F31", { "sketchPlane" : qUnion([Q0])});
            skCircle(sketch, "E180", {"center": v(-364.82, 0) * mm, "radius": 12.7 * mm});
            skSolve(sketch);
        }
        {
            var Q0;
            Q0=makeQuery(id+"F31.imprint","IMPRINT",FACE,{"disambiguationData":[TD([[makeQuery(id+"F31.imprint","IMPRINT",EDGE,{"derivedFrom":sQuery(id+"F31.wireOp",EDGE,"E180")}),1.0]])]});
            extrude(context, id + "F32", {"entities" : qUnion([Q0]), "oppositeDirection" : true, "depth" : 6.35 * mm});
        }
        {
            var Q0;
            Q0=sQuery(id+"F0.wireOp",EDGE,"E97");
            cPlane(context, id + "F33", {"entities" : qUnion([Q0]), "cplaneType" : CPlaneType.LINE_ANGLE, "offset" : 25.4 * mm, "angle" : 0 * degree, "width" : 152.4 * mm, "height" : 152.4 * mm});
        }
        {
            var Q0;
            Q0=qCreatedBy(id+"F33.planeOp",FACE);
            var sketch = newSketch(context, id + "F34", { "sketchPlane" : qUnion([Q0])});
            skLineSegment(sketch, "E181", {"start": v(346.97, -24) * mm, "end": v(364.93, -41.96) * mm});
            skLineSegment(sketch, "E182", {"start": v(346.97, -24) * mm, "end": v(346.27, -24.7) * mm});
            skLineSegment(sketch, "E183", {"start": v(346.27, -24.7) * mm, "end": v(364.23, -42.66) * mm});
            skLineSegment(sketch, "E184", {"start": v(364.23, -42.66) * mm, "end": v(364.93, -41.96) * mm});
            skSolve(sketch);
        }
        {
            var Q0;
            Q0=makeQuery(id+"F34.imprint","IMPRINT",FACE,{"disambiguationData":[TD([[makeQuery(id+"F34.imprint","IMPRINT",EDGE,{"derivedFrom":sQuery(id+"F34.wireOp",EDGE,"E181")}),-1.0]])]});
            extrude(context, id + "F35", {"entities" : qUnion([Q0]), "endBound" : BoundingType.SYMMETRIC, "depth" : 25.4 * mm});
        }
        {
            var Q0;
            {var subQ0=sQuery(id+"F0.wireOp",EDGE,"E100.left");Q0=makeQuery(id+"F0.imprint","IMPRINT",FACE,{"disambiguationData":[TD([[makeQuery(id+"F0.imprint","IMPRINT",EDGE,{"derivedFrom":subQ0}),1.0]])]});}
            var Q1;
            Q1=sQuery(id+"F0.wireOp",EDGE,"E81");
            revolve(context, id + "F36", {"entities" : qUnion([Q0]), "axis" : qUnion([Q1]), "revolveType" : RevolveType.FULL});
        }
        {
            var Q0;
            Q0=makeQuery(id+"F36.opRevolve","SWEPT_FACE",FACE,{"disambiguationData":[OSD([sQuery(id+"F0.wireOp",EDGE,"E101.bottom")])]});
            var sketch = newSketch(context, id + "F37", { "sketchPlane" : qUnion([Q0])});
            skLineSegment(sketch, "E185", {"start": v(-330.2, 0) * mm, "end": v(-314.68, -26.88) * mm, "construction": true});
            skLineSegment(sketch, "E186", {"start": v(-319.44, -18.63) * mm, "end": v(-320.93, -19.49) * mm});
            skLineSegment(sketch, "E187", {"start": v(-320.93, -19.49) * mm, "end": v(-322.2, -17.29) * mm});
            skLineSegment(sketch, "E188", {"start": v(-322.2, -17.29) * mm, "end": v(-322.2, -13.86) * mm});
            skLineSegment(sketch, "E189", {"start": v(-322.2, -13.86) * mm, "end": v(-319.44, -18.63) * mm});
            skLineSegment(sketch, "E190.MirrorCS", {"start": v(-319.44, -18.63) * mm, "end": v(-317.96, -17.77) * mm});
            skLineSegment(sketch, "E191.MirrorCS", {"start": v(-317.96, -17.77) * mm, "end": v(-319.23, -15.57) * mm});
            skLineSegment(sketch, "E192.MirrorCS", {"start": v(-319.23, -15.57) * mm, "end": v(-322.2, -13.86) * mm});
            skLineSegment(sketch, "E193", {"start": v(-330.2, -40.55) * mm, "end": v(-330.2, 40.55) * mm, "construction": true});
            skLineSegment(sketch, "E194.MirrorCS", {"start": v(-339.47, -19.49) * mm, "end": v(-338.2, -17.29) * mm});
            skLineSegment(sketch, "E195.MirrorCS", {"start": v(-340.96, -18.63) * mm, "end": v(-339.47, -19.49) * mm});
            skLineSegment(sketch, "E196.MirrorCS", {"start": v(-340.96, -18.63) * mm, "end": v(-342.44, -17.77) * mm});
            skLineSegment(sketch, "E197.MirrorCS", {"start": v(-342.44, -17.77) * mm, "end": v(-341.17, -15.57) * mm});
            skLineSegment(sketch, "E198.MirrorCS", {"start": v(-341.17, -15.57) * mm, "end": v(-338.2, -13.86) * mm});
            skLineSegment(sketch, "E199.MirrorCS", {"start": v(-338.2, -17.29) * mm, "end": v(-338.2, -13.86) * mm});
            skLineSegment(sketch, "E200.MirrorCS", {"start": v(-317.96, 17.77) * mm, "end": v(-319.23, 15.57) * mm});
            skLineSegment(sketch, "E201.MirrorCS", {"start": v(-319.44, 18.63) * mm, "end": v(-317.96, 17.77) * mm});
            skLineSegment(sketch, "E202.MirrorCS", {"start": v(-319.44, 18.63) * mm, "end": v(-320.93, 19.49) * mm});
            skLineSegment(sketch, "E203.MirrorCS", {"start": v(-320.93, 19.49) * mm, "end": v(-322.2, 17.29) * mm});
            skLineSegment(sketch, "E204.MirrorCS", {"start": v(-322.2, 17.29) * mm, "end": v(-322.2, 13.86) * mm});
            skLineSegment(sketch, "E205.MirrorCS", {"start": v(-319.23, 15.57) * mm, "end": v(-322.2, 13.86) * mm});
            skLineSegment(sketch, "E206.MirrorCS", {"start": v(-338.2, 17.29) * mm, "end": v(-338.2, 13.86) * mm});
            skLineSegment(sketch, "E207.MirrorCS", {"start": v(-341.17, 15.57) * mm, "end": v(-338.2, 13.86) * mm});
            skLineSegment(sketch, "E208.MirrorCS", {"start": v(-342.44, 17.77) * mm, "end": v(-341.17, 15.57) * mm});
            skLineSegment(sketch, "E209.MirrorCS", {"start": v(-340.96, 18.63) * mm, "end": v(-342.44, 17.77) * mm});
            skLineSegment(sketch, "E210.MirrorCS", {"start": v(-340.96, 18.63) * mm, "end": v(-339.47, 19.49) * mm});
            skLineSegment(sketch, "E211.MirrorCS", {"start": v(-339.47, 19.49) * mm, "end": v(-338.2, 17.29) * mm});
            skLineSegment(sketch, "E212", {"start": v(-330.2, 0) * mm, "end": v(-306.18, -13.87) * mm, "construction": true});
            skLineSegment(sketch, "E213.MirrorCS", {"start": v(-308.69, 0) * mm, "end": v(-308.69, -1.72) * mm});
            skLineSegment(sketch, "E214.MirrorCS", {"start": v(-308.69, -1.72) * mm, "end": v(-311.23, -1.72) * mm});
            skLineSegment(sketch, "E215.MirrorCS", {"start": v(-311.23, -1.72) * mm, "end": v(-314.2, 0) * mm});
            skLineSegment(sketch, "E216.MirrorCS", {"start": v(-308.69, 0) * mm, "end": v(-308.69, 1.72) * mm});
            skLineSegment(sketch, "E217.MirrorCS", {"start": v(-308.69, 1.72) * mm, "end": v(-311.23, 1.72) * mm});
            skLineSegment(sketch, "E218.MirrorCS", {"start": v(-311.23, 1.72) * mm, "end": v(-314.2, 0) * mm});
            skLineSegment(sketch, "E219.MirrorCS", {"start": v(-349.17, -1.72) * mm, "end": v(-346.2, 0) * mm});
            skLineSegment(sketch, "E220.MirrorCS", {"start": v(-351.71, -1.72) * mm, "end": v(-349.17, -1.72) * mm});
            skLineSegment(sketch, "E221.MirrorCS", {"start": v(-351.71, 0) * mm, "end": v(-351.71, -1.72) * mm});
            skLineSegment(sketch, "E222.MirrorCS", {"start": v(-351.71, 0) * mm, "end": v(-351.71, 1.72) * mm});
            skLineSegment(sketch, "E223.MirrorCS", {"start": v(-351.71, 1.72) * mm, "end": v(-349.17, 1.72) * mm});
            skLineSegment(sketch, "E224.MirrorCS", {"start": v(-349.17, 1.72) * mm, "end": v(-346.2, 0) * mm});
            skSolve(sketch);
        }
        {
            var Q0;
            {var subQ0=sQuery(id+"F37.wireOp",EDGE,"E188");Q0=makeQuery(id+"F37.imprint","IMPRINT",FACE,{"disambiguationData":[TD([[makeQuery(id+"F37.imprint","IMPRINT",EDGE,{"derivedFrom":subQ0}),-1.0]])]});}
            var Q1;
            {var subQ0=sQuery(id+"F37.wireOp",EDGE,"E192.MirrorCS");Q1=makeQuery(id+"F37.imprint","IMPRINT",FACE,{"disambiguationData":[TD([[makeQuery(id+"F37.imprint","IMPRINT",EDGE,{"derivedFrom":subQ0}),1.0]])]});}
            var Q2;
            {var subQ0=sQuery(id+"F37.wireOp",EDGE,"E198.MirrorCS");Q2=makeQuery(id+"F37.imprint","IMPRINT",FACE,{"disambiguationData":[TD([[makeQuery(id+"F37.imprint","IMPRINT",EDGE,{"derivedFrom":subQ0}),-1.0]])]});}
            var Q3;
            {var subQ0=sQuery(id+"F37.wireOp",EDGE,"E215.MirrorCS");Q3=makeQuery(id+"F37.imprint","IMPRINT",FACE,{"disambiguationData":[TD([[makeQuery(id+"F37.imprint","IMPRINT",EDGE,{"derivedFrom":subQ0}),-1.0]])]});}
            var Q4;
            {var subQ0=sQuery(id+"F37.wireOp",EDGE,"E219.MirrorCS");Q4=makeQuery(id+"F37.imprint","IMPRINT",FACE,{"disambiguationData":[TD([[makeQuery(id+"F37.imprint","IMPRINT",EDGE,{"derivedFrom":subQ0}),1.0]])]});}
            var Q5;
            {var subQ0=sQuery(id+"F37.wireOp",EDGE,"E206.MirrorCS");Q5=makeQuery(id+"F37.imprint","IMPRINT",FACE,{"disambiguationData":[TD([[makeQuery(id+"F37.imprint","IMPRINT",EDGE,{"derivedFrom":subQ0}),-1.0]])]});}
            var Q6;
            {var subQ0=sQuery(id+"F37.wireOp",EDGE,"E204.MirrorCS");Q6=makeQuery(id+"F37.imprint","IMPRINT",FACE,{"disambiguationData":[TD([[makeQuery(id+"F37.imprint","IMPRINT",EDGE,{"derivedFrom":subQ0}),1.0]])]});}
            extrude(context, id + "F38", {"entities" : qUnion([Q0, Q1, Q2, Q3, Q4, Q5, Q6]), "operationType" : NewBodyOperationType.REMOVE, "endBound" : BoundingType.THROUGH_ALL, "oppositeDirection" : true, "depth" : 25.4 * mm});
        }
        {
            var Q0;
            {var subQ5=sQuery(id+"F0.wireOp",EDGE,"E106");Q0=makeQuery(id+"F0.imprint","IMPRINT",FACE,{"disambiguationData":[TD([[makeQuery(id+"F0.imprint","IMPRINT",EDGE,{"derivedFrom":subQ5}),-1.0]])]});}
            var Q1;
            {var subQ1=sQuery(id+"F0.wireOp",EDGE,"E108");Q1=makeQuery(id+"F0.imprint","IMPRINT",FACE,{"disambiguationData":[TD([[makeQuery(id+"F0.imprint","IMPRINT",EDGE,{"derivedFrom":subQ1}),-1.0]])]});}
            var Q2;
            Q2=sQuery(id+"F0.wireOp",EDGE,"E81");
            revolve(context, id + "F39", {"entities" : qUnion([Q0, Q1]), "axis" : qUnion([Q2]), "revolveType" : RevolveType.FULL});
        }
        {
            var Q0;
            Q0=sQuery(id+"F0.wireOp",EDGE,"E111");
            cPlane(context, id + "F40", {"entities" : qUnion([Q0]), "cplaneType" : CPlaneType.LINE_ANGLE, "offset" : 25.4 * mm, "angle" : 0 * degree, "width" : 152.4 * mm, "height" : 152.4 * mm});
        }
        {
            var Q0;
            Q0=qCreatedBy(id+"F40.planeOp",FACE);
            var sketch = newSketch(context, id + "F41", { "sketchPlane" : qUnion([Q0])});
            skLineSegment(sketch, "E225.bottom", {"start": v(-292.1, 12.7) * mm, "end": v(-368.3, 12.7) * mm});
            skLineSegment(sketch, "E225.top", {"start": v(-292.1, -12.7) * mm, "end": v(-368.3, -12.7) * mm});
            skLineSegment(sketch, "E225.left", {"start": v(-292.1, 12.7) * mm, "end": v(-292.1, -12.7) * mm});
            skLineSegment(sketch, "E225.right", {"start": v(-368.3, 12.7) * mm, "end": v(-368.3, -12.7) * mm});
            skSolve(sketch);
        }
        {
            var Q0;
            Q0=makeQuery(id+"F41.imprint","IMPRINT",FACE,{"disambiguationData":[TD([[makeQuery(id+"F41.imprint","IMPRINT",EDGE,{"derivedFrom":sQuery(id+"F41.wireOp",EDGE,"E225.bottom")}),1.0]])]});
            extrude(context, id + "F42", {"entities" : qUnion([Q0]), "depth" : 2 * mm});
        }
        {
            var Q0;
            Q0=makeQuery(id+"F9.opRevolve","SWEPT_FACE",FACE,{"disambiguationData":[OSD([sQuery(id+"F0.wireOp",EDGE,"E39")])]});
            var sketch = newSketch(context, id + "F43", { "sketchPlane" : qUnion([Q0])});
            skCircle(sketch, "E226", {"center": v(101.6, 0) * mm, "radius": 1 * mm});
            skSolve(sketch);
        }
        {
            var Q0;
            Q0 = qSketchRegion(id + "F43", true);
            var Q1;
            Q1=sQuery(id+"F0.wireOp",EDGE,"E112");
            var Q2;
            Q2=sQuery(id+"F0.wireOp",EDGE,"E115");
            sweep(context, id + "F44", {"profiles" : qUnion([Q0]), "path" : qUnion([Q1, Q2])});
        }
        {
            var Q0;
            Q0=makeQuery(id+"F44.opSweep","CAP_FACE",FACE,{"disambiguationData":[OSD([sQuery(id+"F0.wireOp",VERTEX,"E115.end"),sQuery(id+"F43.wireOp",EDGE,"E226")])],"isStart":false});
            var Q1;
            Q1=makeQuery(id+"F44.opSweep","CAP_EDGE",EDGE,{"disambiguationData":[OSD([sQuery(id+"F0.wireOp",VERTEX,"E115.end"),sQuery(id+"F43.wireOp",EDGE,"E226")])],"isStart":false});
            var Q2;
            Q2=sQuery(id+"F0.wireOp",EDGE,"E113");
            sweep(context, id + "F45", {"operationType" : NewBodyOperationType.ADD, "profiles" : qUnion([Q0]), "surfaceProfiles" : qUnion([Q1]), "path" : qUnion([Q2])});
        }
        {
            var Q0;
            Q0=makeQuery(id+"F0.imprint","IMPRINT",FACE,{"disambiguationData":[TD([[makeQuery(id+"F0.imprint","IMPRINT",EDGE,{"derivedFrom":sQuery(id+"F0.wireOp",EDGE,"E116")}),1.0]])]});
            var Q1;
            Q1=makeQuery(id+"F0.imprint","IMPRINT",FACE,{"disambiguationData":[TD([[makeQuery(id+"F0.imprint","IMPRINT",EDGE,{"derivedFrom":sQuery(id+"F0.wireOp",EDGE,"E133")}),-1.0]])]});
            var Q2;
            Q2=makeQuery(id+"F0.imprint","IMPRINT",FACE,{"disambiguationData":[TD([[makeQuery(id+"F0.imprint","IMPRINT",EDGE,{"derivedFrom":sQuery(id+"F0.wireOp",EDGE,"E125")}),-1.0]])]});
            var Q3;
            Q3=makeQuery(id+"F0.imprint","IMPRINT",FACE,{"disambiguationData":[TD([[makeQuery(id+"F0.imprint","IMPRINT",EDGE,{"derivedFrom":sQuery(id+"F0.wireOp",EDGE,"E141")}),-1.0]])]});
            extrude(context, id + "F46", {"entities" : qUnion([Q0, Q1, Q2, Q3]), "depth" : 2 * mm});
        }
        {
            var Q0;
            Q0=makeQuery(id+"F0.imprint","IMPRINT",FACE,{"disambiguationData":[TD([[makeQuery(id+"F0.imprint","IMPRINT",EDGE,{"derivedFrom":sQuery(id+"F0.wireOp",EDGE,"E165")}),-1.0]])]});
            var Q1;
            Q1=makeQuery(id+"F0.imprint","IMPRINT",FACE,{"disambiguationData":[TD([[makeQuery(id+"F0.imprint","IMPRINT",EDGE,{"derivedFrom":sQuery(id+"F0.wireOp",EDGE,"E157")}),-1.0]])]});
            var Q2;
            Q2=makeQuery(id+"F0.imprint","IMPRINT",FACE,{"disambiguationData":[TD([[makeQuery(id+"F0.imprint","IMPRINT",EDGE,{"derivedFrom":sQuery(id+"F0.wireOp",EDGE,"E149")}),-1.0]])]});
            extrude(context, id + "F47", {"entities" : qUnion([Q0, Q1, Q2]), "depth" : 2 * mm});
        }
        {
            var Q0;
            Q0=makeQuery(id+"F19.opRevolve","SWEPT_FACE",FACE,{"disambiguationData":[OSD([sQuery(id+"F0.wireOp",EDGE,"E85")])]});
            cPlane(context, id + "F48", {"entities" : qUnion([Q0]), "cplaneType" : CPlaneType.OFFSET, "offset" : 12.7 * mm, "width" : 152.4 * mm, "height" : 152.4 * mm});
        }
        {
            var Q0;
            Q0=qCreatedBy(id+"F48.planeOp",FACE);
            var sketch = newSketch(context, id + "F49", { "sketchPlane" : qUnion([Q0])});
            skCircle(sketch, "E227", {"center": v(-58.73, 0) * mm, "radius": 12.7 * mm});
            skCircle(sketch, "E228", {"center": v(-58.73, 0) * mm, "radius": 2.54 * mm});
            skSolve(sketch);
        }
        {
            var Q0;
            Q0=makeQuery(id+"F49.imprint","IMPRINT",FACE,{"disambiguationData":[TD([[makeQuery(id+"F49.imprint","IMPRINT",EDGE,{"derivedFrom":sQuery(id+"F49.wireOp",EDGE,"E227")}),1.0]])]});
            extrude(context, id + "F50", {"entities" : qUnion([Q0]), "depth" : 5.08 * mm});
        }
        {
            var Q0;
            Q0=makeQuery(id+"F19.opRevolve","SWEPT_FACE",FACE,{"disambiguationData":[OSD([sQuery(id+"F0.wireOp",EDGE,"E89")])]});
            cPlane(context, id + "F51", {"entities" : qUnion([Q0]), "cplaneType" : CPlaneType.OFFSET, "offset" : 25.4 * mm, "oppositeDirection" : true, "width" : 152.4 * mm, "height" : 152.4 * mm});
        }
        {
            var Q0;
            Q0=qCreatedBy(id+"F51.planeOp",FACE);
            var sketch = newSketch(context, id + "F52", { "sketchPlane" : qUnion([Q0])});
            skCircle(sketch, "E229", {"center": v(-58.73, 0) * mm, "radius": 12.7 * mm});
            skSolve(sketch);
        }
        {
            var Q0;
            Q0=makeQuery(id+"F52.imprint","IMPRINT",FACE,{"disambiguationData":[TD([[makeQuery(id+"F52.imprint","IMPRINT",EDGE,{"derivedFrom":sQuery(id+"F52.wireOp",EDGE,"E229")}),1.0]])]});
            extrude(context, id + "F53", {"entities" : qUnion([Q0]), "depth" : 4 * mm});
        }
        {
            var Q0;
            Q0 = qSketchRegion(id + "F52", true);
            extrude(context, id + "F54", {"entities" : qUnion([Q0]), "oppositeDirection" : true, "depth" : 4 * mm});
        }
        {
            var Q0;
            Q0=makeQuery(id+"F16.opRevolve","SWEPT_FACE",FACE,{"disambiguationData":[OSD([sQuery(id+"F0.wireOp",EDGE,"E52")])]});
            cPlane(context, id + "F55", {"entities" : qUnion([Q0]), "cplaneType" : CPlaneType.OFFSET, "offset" : 25.4 * mm, "oppositeDirection" : true, "width" : 152.4 * mm, "height" : 152.4 * mm});
        }
        {
            var Q0;
            Q0=qCreatedBy(id+"F55.planeOp",FACE);
            var sketch = newSketch(context, id + "F56", { "sketchPlane" : qUnion([Q0])});
            skCircle(sketch, "E230", {"center": v(-152.4, 0) * mm, "radius": 12.7 * mm});
            skSolve(sketch);
        }
        {
            var Q0;
            Q0=makeQuery(id+"F56.imprint","IMPRINT",FACE,{"disambiguationData":[TD([[makeQuery(id+"F56.imprint","IMPRINT",EDGE,{"derivedFrom":sQuery(id+"F56.wireOp",EDGE,"E230")}),1.0]])]});
            extrude(context, id + "F57", {"entities" : qUnion([Q0]), "depth" : 4 * mm});
        }
        {
            var Q0;
            Q0 = qSketchRegion(id + "F56", true);
            extrude(context, id + "F58", {"entities" : qUnion([Q0]), "oppositeDirection" : true, "depth" : 4 * mm});
        }
    });
